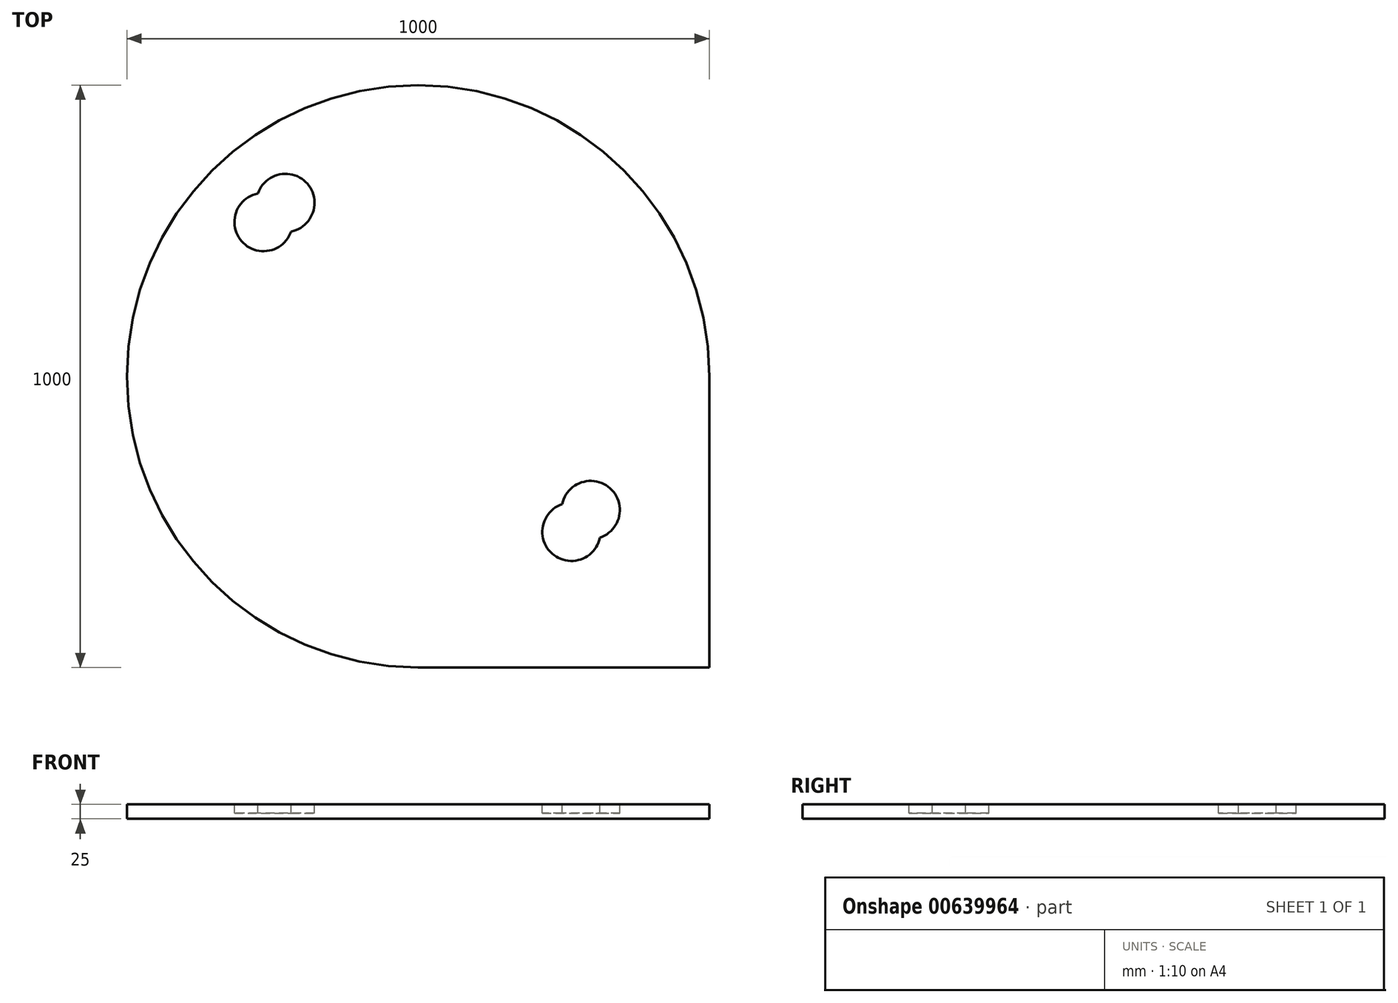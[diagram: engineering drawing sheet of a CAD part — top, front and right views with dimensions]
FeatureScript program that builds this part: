
annotation { "Feature Type Name" : "Feature", "Feature Type Description" : "" }
export const myFeature = defineFeature(function(context is Context, id is Id, definition is map)
    precondition{}
    {
        {
            var Q0;
            Q0=qCreatedBy(makeId("Top.planeOp"),FACE);
            var sketch = newSketch(context, id + "F0", { "sketchPlane" : qUnion([Q0])});
            skArc(sketch, "E0", {"start": v(500, 0) * mm, "mid": v(-353.55, 353.55) * mm, "end": v(0, -500) * mm});
            skLineSegment(sketch, "E1", {"start": v(500, 0) * mm, "end": v(500, -500) * mm});
            skLineSegment(sketch, "E2", {"start": v(0, -500) * mm, "end": v(500, -500) * mm});
            skSolve(sketch);
        }
        {
            var Q0;
            Q0=makeQuery(id+"F0.imprint","IMPRINT",FACE,{"disambiguationData":[TD([[makeQuery(id+"F0.imprint","IMPRINT",EDGE,{"derivedFrom":sQuery(id+"F0.wireOp",EDGE,"E0")}),1.0]])]});
            extrude(context, id + "F1", {"entities" : qUnion([Q0]), "depth" : 25 * mm, "offsetDistance" : 25 * mm});
        }
        {
            var Q0;
            Q0=makeQuery(id+"F1.opExtrude","CAP_FACE",FACE,{"disambiguationData":[OSD([sQuery(id+"F0.wireOp",EDGE,"E0")])],"isStart":false});
            var sketch = newSketch(context, id + "F2", { "sketchPlane" : qUnion([Q0])});
            skArc(sketch, "E3", {"start": v(-218.05, 248.85) * mm, "mid": v(-190.18, 330.84) * mm, "end": v(-275.12, 313.99) * mm});
            skArc(sketch, "E4", {"start": v(247.53, -219.54) * mm, "mid": v(230.16, -304.38) * mm, "end": v(312.32, -277) * mm});
            skArc(sketch, "E5", {"start": v(-275.12, 313.99) * mm, "mid": v(-303, 232) * mm, "end": v(-218.05, 248.85) * mm});
            skArc(sketch, "E6", {"start": v(312.32, -277) * mm, "mid": v(329.7, -192.16) * mm, "end": v(247.53, -219.54) * mm});
            skCircle(sketch, "E7", {"center": v(0, 0) * mm, "radius": 375 * mm});
            skSolve(sketch);
        }
        {
            var Q0;
            Q0=makeQuery(id+"F2.imprint","IMPRINT",FACE,{"disambiguationData":[TD([[makeQuery(id+"F2.imprint","IMPRINT",EDGE,{"derivedFrom":sQuery(id+"F2.wireOp",EDGE,"E3")}),1.0]])]});
            var Q1;
            Q1=makeQuery(id+"F2.imprint","IMPRINT",FACE,{"disambiguationData":[TD([[makeQuery(id+"F2.imprint","IMPRINT",EDGE,{"derivedFrom":sQuery(id+"F2.wireOp",EDGE,"E4")}),1.0]])]});
            extrude(context, id + "F3", {"entities" : qUnion([Q0, Q1]), "operationType" : NewBodyOperationType.REMOVE, "oppositeDirection" : true, "depth" : 15 * mm, "offsetDistance" : 25 * mm});
        }
    });
